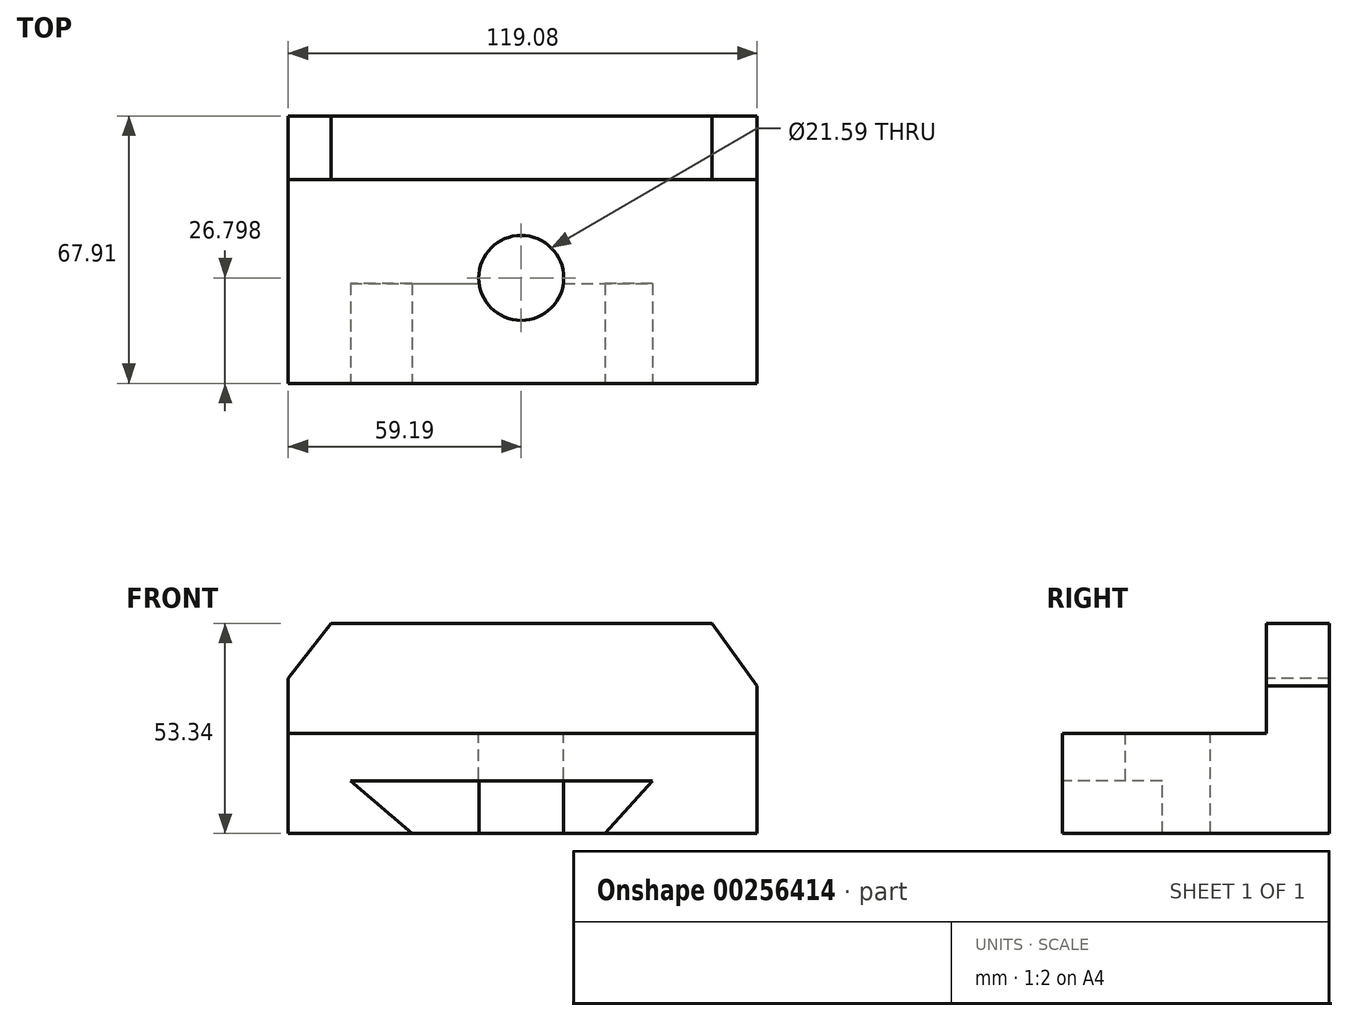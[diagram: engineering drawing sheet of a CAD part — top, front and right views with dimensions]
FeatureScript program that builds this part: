
annotation { "Feature Type Name" : "Feature", "Feature Type Description" : "" }
export const myFeature = defineFeature(function(context is Context, id is Id, definition is map)
    precondition{}
    {
        {
            var Q0;
            Q0=qCreatedBy(makeId("Top.planeOp"),FACE);
            var sketch = newSketch(context, id + "F0", { "sketchPlane" : qUnion([Q0])});
            skLineSegment(sketch, "E0.bottom", {"start": v(-59.2, 25.58) * mm, "end": v(59.9, 25.58) * mm});
            skLineSegment(sketch, "E0.top", {"start": v(-59.2, -42.33) * mm, "end": v(59.9, -42.33) * mm});
            skLineSegment(sketch, "E0.left", {"start": v(-59.2, 25.58) * mm, "end": v(-59.2, -42.33) * mm});
            skLineSegment(sketch, "E0.right", {"start": v(59.9, 25.58) * mm, "end": v(59.9, -42.33) * mm});
            skSolve(sketch);
        }
        {
            var Q0;
            Q0=makeQuery(id+"F0.imprint","IMPRINT",FACE,{"disambiguationData":[TD([[makeQuery(id+"F0.imprint","IMPRINT",EDGE,{"derivedFrom":sQuery(id+"F0.wireOp",EDGE,"E0.bottom")}),-1.0]])]});
            extrude(context, id + "F1", {"entities" : qUnion([Q0]), "depth" : 25.4 * mm});
        }
        {
            var Q0;
            Q0=makeQuery(id+"F1.opExtrude","SWEPT_FACE",FACE,{"disambiguationData":[OSD([sQuery(id+"F0.wireOp",EDGE,"E0.top")])]});
            var sketch = newSketch(context, id + "F2", { "sketchPlane" : qUnion([Q0])});
            skLineSegment(sketch, "E1", {"start": v(-27.8, 0) * mm, "end": v(-43.38, 13.39) * mm});
            skLineSegment(sketch, "E2", {"start": v(-43.38, 13.39) * mm, "end": v(33.38, 13.39) * mm});
            skLineSegment(sketch, "E3", {"start": v(33.38, 13.39) * mm, "end": v(21.28, 0) * mm});
            skLineSegment(sketch, "E4", {"start": v(21.28, 0) * mm, "end": v(-27.8, 0) * mm});
            skSolve(sketch);
        }
        {
            var Q0;
            Q0=makeQuery(id+"F2.imprint","IMPRINT",FACE,{"disambiguationData":[TD([[makeQuery(id+"F2.imprint","IMPRINT",EDGE,{"derivedFrom":sQuery(id+"F2.wireOp",EDGE,"E1")}),-1.0]])]});
            extrude(context, id + "F3", {"entities" : qUnion([Q0]), "operationType" : NewBodyOperationType.REMOVE, "oppositeDirection" : true, "depth" : 25.4 * mm});
        }
        {
            var Q0;
            Q0=makeQuery(id+"F1.opExtrude","CAP_FACE",FACE,{"disambiguationData":[OSD([sQuery(id+"F0.wireOp",EDGE,"E0.bottom"),sQuery(id+"F0.wireOp",EDGE,"E0.top"),sQuery(id+"F0.wireOp",EDGE,"E0.left"),sQuery(id+"F0.wireOp",EDGE,"E0.right")])],"isStart":false});
            var sketch = newSketch(context, id + "F4", { "sketchPlane" : qUnion([Q0])});
            skLineSegment(sketch, "E5.bottom", {"start": v(-59.2, 25.58) * mm, "end": v(59.9, 25.58) * mm});
            skLineSegment(sketch, "E5.top", {"start": v(-59.2, 9.47) * mm, "end": v(59.9, 9.47) * mm});
            skLineSegment(sketch, "E5.left", {"start": v(-59.2, 25.58) * mm, "end": v(-59.2, 9.47) * mm});
            skLineSegment(sketch, "E5.right", {"start": v(59.9, 25.58) * mm, "end": v(59.9, 9.47) * mm});
            skSolve(sketch);
        }
        {
            var Q0;
            Q0=makeQuery(id+"F4.imprint","IMPRINT",FACE,{"disambiguationData":[TD([[makeQuery(id+"F4.imprint","IMPRINT",EDGE,{"derivedFrom":sQuery(id+"F4.wireOp",EDGE,"E5.bottom")}),-1.0]])]});
            extrude(context, id + "F5", {"entities" : qUnion([Q0]), "operationType" : NewBodyOperationType.ADD, "depth" : 27.94 * mm});
        }
        {
            var Q0;
            Q0=makeQuery(id+"F5.opExtrude","SWEPT_FACE",FACE,{"disambiguationData":[OSD([sQuery(id+"F4.wireOp",EDGE,"E5.top")])]});
            var sketch = newSketch(context, id + "F6", { "sketchPlane" : qUnion([Q0])});
            skLineSegment(sketch, "E6", {"start": v(-48.26, 53.34) * mm, "end": v(-59.2, 39.37) * mm});
            skSolve(sketch);
        }
        {
            var Q0;
            {var subQ0=sQuery(id+"F6.wireOp",EDGE,"E6");Q0=makeQuery(id+"F6.imprint","IMPRINT",FACE,{"disambiguationData":[TD([[makeQuery(id+"F6.imprint","IMPRINT",EDGE,{"derivedFrom":subQ0}),-1.0]])]});}
            extrude(context, id + "F7", {"entities" : qUnion([Q0]), "operationType" : NewBodyOperationType.REMOVE, "oppositeDirection" : true, "depth" : 25.4 * mm});
        }
        {
            var Q0;
            Q0=makeQuery(id+"F5.opExtrude","SWEPT_FACE",FACE,{"disambiguationData":[OSD([sQuery(id+"F4.wireOp",EDGE,"E5.top")])]});
            var sketch = newSketch(context, id + "F8", { "sketchPlane" : qUnion([Q0])});
            skLineSegment(sketch, "E7", {"start": v(48.5, 53.34) * mm, "end": v(59.9, 37.45) * mm});
            skSolve(sketch);
        }
        {
            var Q0;
            {var subQ0=sQuery(id+"F8.wireOp",EDGE,"E7");Q0=makeQuery(id+"F8.imprint","IMPRINT",FACE,{"disambiguationData":[TD([[makeQuery(id+"F8.imprint","IMPRINT",EDGE,{"derivedFrom":subQ0}),1.0]])]});}
            extrude(context, id + "F9", {"entities" : qUnion([Q0]), "operationType" : NewBodyOperationType.REMOVE, "oppositeDirection" : true, "depth" : 25.4 * mm});
        }
        {
            var Q0;
            Q0=makeQuery(id+"F1.opExtrude","CAP_FACE",FACE,{"disambiguationData":[OSD([sQuery(id+"F0.wireOp",EDGE,"E0.bottom"),sQuery(id+"F0.wireOp",EDGE,"E0.top"),sQuery(id+"F0.wireOp",EDGE,"E0.left"),sQuery(id+"F0.wireOp",EDGE,"E0.right")])],"isStart":false});
            var sketch = newSketch(context, id + "F10", { "sketchPlane" : qUnion([Q0])});
            skCircle(sketch, "E8", {"center": v(0, -15.2) * mm, "radius": 11.3 * mm});
            skSolve(sketch);
        }
        {
            var Q0;
            Q0=makeQuery(id+"F10.imprint","IMPRINT",FACE,{"disambiguationData":[TD([[makeQuery(id+"F10.imprint","IMPRINT",EDGE,{"derivedFrom":sQuery(id+"F10.wireOp",EDGE,"E8")}),-1.0]])]});
            var sketch = newSketch(context, id + "F11", { "sketchPlane" : qUnion([Q0])});
            skLineSegment(sketch, "E9", {"start": v(0, -15.53) * mm, "end": v(39.89, -15.53) * mm});
            skLineSegment(sketch, "E10", {"start": v(0, -15.53) * mm, "end": v(-41.05, -15.53) * mm});
            skLineSegment(sketch, "E11", {"start": v(0, -15.53) * mm, "end": v(0, 24.27) * mm});
            skLineSegment(sketch, "E12", {"start": v(0, -15.53) * mm, "end": v(0, -60.92) * mm});
            skSolve(sketch);
        }
        {
            var Q0;
            Q0=sQuery(id+"F11.wireOp",VERTEX,"E12.start");
            var Q1;
            Q1=makeQuery(id+"F1.opExtrude","SWEPT_BODY",BODY,{"disambiguationData":[OSD([sQuery(id+"F0.wireOp",EDGE,"E0.bottom"),sQuery(id+"F0.wireOp",EDGE,"E0.top"),sQuery(id+"F0.wireOp",EDGE,"E0.left"),sQuery(id+"F0.wireOp",EDGE,"E0.right")])]});
            hole(context, id + "F12", {"style" : HoleStyle.SIMPLE, "endStyle" : HoleEndStyle.THROUGH, "holeDiameter" : 21.59 * mm, "tappedDepth" : 12.7 * mm, "tapClearance" : 3, "locations" : qUnion([Q0]), "scope" : qUnion([Q1])});
        }
    });
